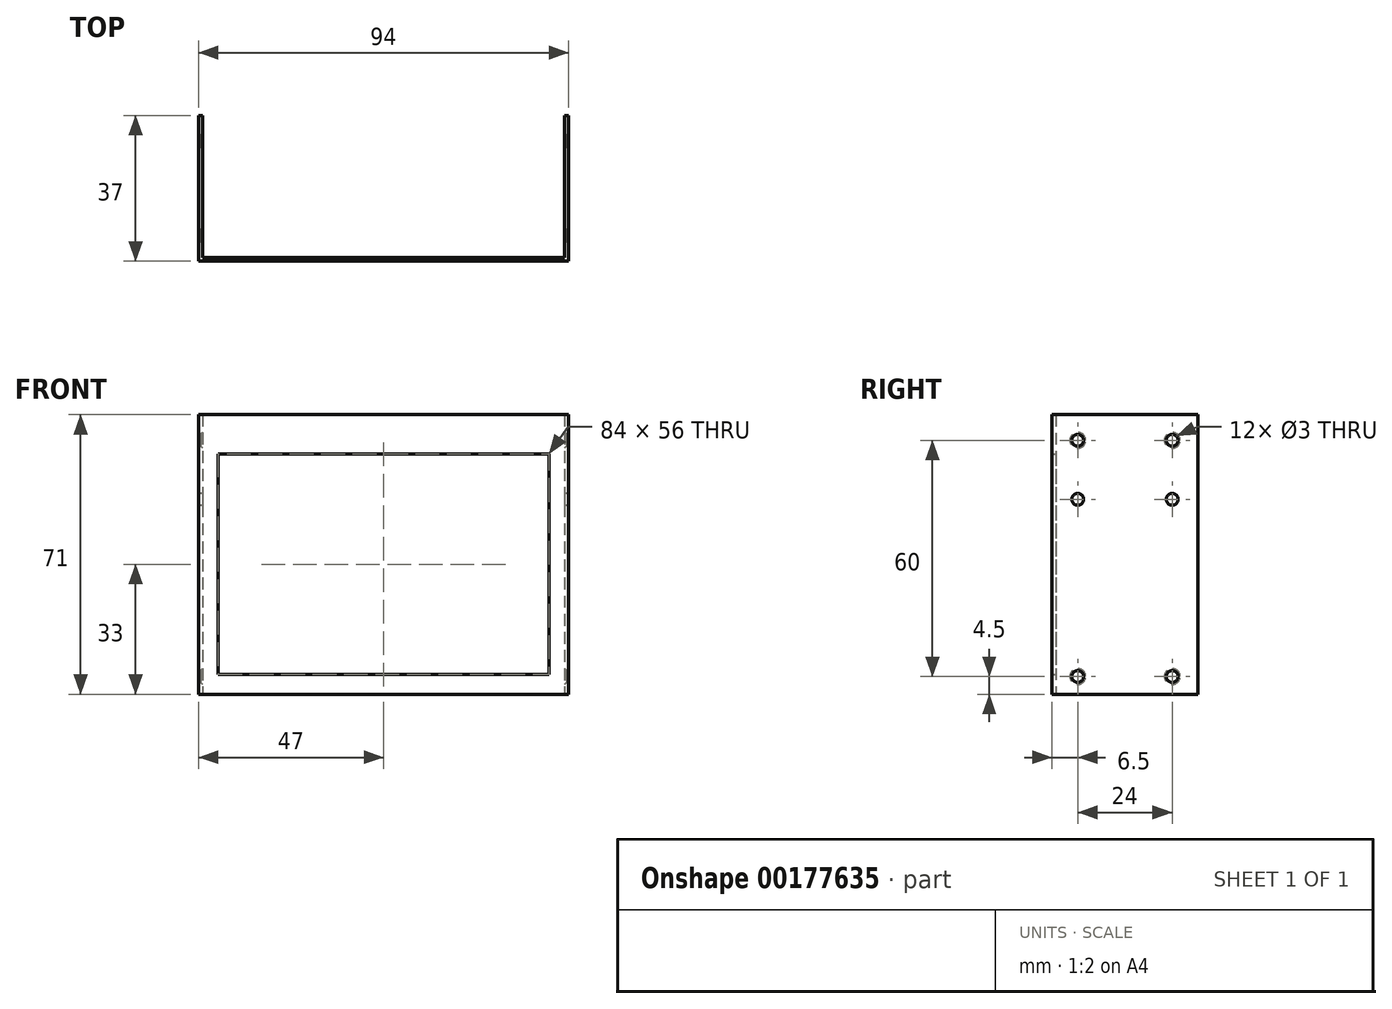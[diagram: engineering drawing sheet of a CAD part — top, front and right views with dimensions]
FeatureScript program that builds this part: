
annotation { "Feature Type Name" : "Feature", "Feature Type Description" : "" }
export const myFeature = defineFeature(function(context is Context, id is Id, definition is map)
    precondition{}
    {
        {
            var Q0;
            Q0=qCreatedBy(makeId("Front.planeOp"),FACE);
            var sketch = newSketch(context, id + "F0", { "sketchPlane" : qUnion([Q0])});
            skLineSegment(sketch, "E0.bottom", {"start": v(47, 35.5) * mm, "end": v(-47, 35.5) * mm});
            skLineSegment(sketch, "E0.top", {"start": v(47, -35.5) * mm, "end": v(-47, -35.5) * mm});
            skLineSegment(sketch, "E0.left", {"start": v(47, 35.5) * mm, "end": v(47, -35.5) * mm});
            skLineSegment(sketch, "E0.right", {"start": v(-47, 35.5) * mm, "end": v(-47, -35.5) * mm});
            skPoint(sketch, "E0.middle", {"position": v(0, 0) * mm});
            skLineSegment(sketch, "E1.bottom", {"start": v(42, 25.5) * mm, "end": v(-42, 25.5) * mm});
            skLineSegment(sketch, "E1.top", {"start": v(42, -30.5) * mm, "end": v(-42, -30.5) * mm});
            skLineSegment(sketch, "E1.left", {"start": v(42, 25.5) * mm, "end": v(42, -30.5) * mm});
            skLineSegment(sketch, "E1.right", {"start": v(-42, 25.5) * mm, "end": v(-42, -30.5) * mm});
            skPoint(sketch, "E1.middle", {"position": v(0, -2.5) * mm});
            skSolve(sketch);
        }
        {
            var Q0;
            Q0=qSketchRegion(id+"F0",true);
            extrude(context, id + "F1", {"entities" : qUnion([Q0]), "depth" : 1 * mm});
        }
        {
            var Q0;
            Q0=makeQuery(id+"F1.opExtrude","CAP_FACE",FACE,{"disambiguationData":[OSD([sQuery(id+"F0.wireOp",EDGE,"E0.bottom"),sQuery(id+"F0.wireOp",EDGE,"E0.top"),sQuery(id+"F0.wireOp",EDGE,"E0.left"),sQuery(id+"F0.wireOp",EDGE,"E0.right"),sQuery(id+"F0.wireOp",EDGE,"SgeA5SFv-ycm6-KkIP-0Kqd-vPRJc91bn5sW.bottom"),sQuery(id+"F0.wireOp",EDGE,"SgeA5SFv-ycm6-KkIP-0Kqd-vPRJc91bn5sW.top"),sQuery(id+"F0.wireOp",EDGE,"SgeA5SFv-ycm6-KkIP-0Kqd-vPRJc91bn5sW.left"),sQuery(id+"F0.wireOp",EDGE,"SgeA5SFv-ycm6-KkIP-0Kqd-vPRJc91bn5sW.right")])],"isStart":true});
            var sketch = newSketch(context, id + "F2", { "sketchPlane" : qUnion([Q0])});
            skLineSegment(sketch, "E2.bottom", {"start": v(-47, 35.5) * mm, "end": v(-46, 35.5) * mm});
            skLineSegment(sketch, "E2.top", {"start": v(-47, -35.5) * mm, "end": v(-46, -35.5) * mm});
            skLineSegment(sketch, "E2.left", {"start": v(-47, 35.5) * mm, "end": v(-47, -35.5) * mm});
            skLineSegment(sketch, "E2.right", {"start": v(-46, 35.5) * mm, "end": v(-46, -35.5) * mm});
            skLineSegment(sketch, "E3.bottom", {"start": v(47, 35.5) * mm, "end": v(46, 35.5) * mm});
            skLineSegment(sketch, "E3.top", {"start": v(47, -35.5) * mm, "end": v(46, -35.5) * mm});
            skLineSegment(sketch, "E3.left", {"start": v(47, 35.5) * mm, "end": v(47, -35.5) * mm});
            skLineSegment(sketch, "E3.right", {"start": v(46, 35.5) * mm, "end": v(46, -35.5) * mm});
            skSolve(sketch);
        }
        {
            var Q0;
            Q0=qSketchRegion(id+"F2",true);
            extrude(context, id + "F3", {"entities" : qUnion([Q0]), "operationType" : NewBodyOperationType.ADD, "depth" : 36 * mm});
        }
        {
            var Q0;
            Q0=makeQuery(id+"F3.boolean.opBoolean","MERGE",FACE,{"derivedFrom":[makeQuery(id+"F1.opExtrude","SWEPT_FACE",FACE,{"disambiguationData":[OSD([sQuery(id+"F0.wireOp",EDGE,"E0.right")])]}),makeQuery(id+"F3.opExtrude","SWEPT_FACE",FACE,{"disambiguationData":[OSD([sQuery(id+"F2.wireOp",EDGE,"E3.left")])]})]});
            var sketch = newSketch(context, id + "F4", { "sketchPlane" : qUnion([Q0])});
            skCircle(sketch, "E4", {"center": v(-29.5, -31) * mm, "radius": 1.5 * mm});
            skCircle(sketch, "E5", {"center": v(-5.5, -31) * mm, "radius": 1.5 * mm});
            skCircle(sketch, "E6", {"center": v(-29.5, 29) * mm, "radius": 1.5 * mm});
            skCircle(sketch, "E7", {"center": v(-5.5, 29) * mm, "radius": 1.5 * mm});
            skLineSegment(sketch, "E8", {"start": v(-29.5, 29) * mm, "end": v(-29.5, -31) * mm, "construction": true});
            skLineSegment(sketch, "E9", {"start": v(-5.5, 29) * mm, "end": v(-5.5, -31) * mm, "construction": true});
            skCircle(sketch, "E10", {"center": v(-29.5, 14) * mm, "radius": 1.5 * mm});
            skCircle(sketch, "E11", {"center": v(-5.5, 14) * mm, "radius": 1.5 * mm});
            skSolve(sketch);
        }
        {
            var Q0;
            Q0=qSketchRegion(id+"F4",true);
            extrude(context, id + "F5", {"entities" : qUnion([Q0]), "operationType" : NewBodyOperationType.REMOVE, "oppositeDirection" : true, "depth" : 100 * mm});
        }
        {
            var Q0;
            Q0=makeQuery(id+"F5.boolean.opBoolean","INTERSECT",EDGE,{"derivedFrom":[makeQuery(id+"F3.opExtrude","SWEPT_FACE",FACE,{"disambiguationData":[OSD([sQuery(id+"F2.wireOp",EDGE,"E3.right")])]}),makeQuery(id+"F5.opExtrude","SWEPT_FACE",FACE,{"disambiguationData":[OSD([sQuery(id+"F4.wireOp",EDGE,"E4")])]})]});
            var Q1;
            Q1=makeQuery(id+"F5.boolean.opBoolean","INTERSECT",EDGE,{"derivedFrom":[makeQuery(id+"F3.opExtrude","SWEPT_FACE",FACE,{"disambiguationData":[OSD([sQuery(id+"F2.wireOp",EDGE,"E3.right")])]}),makeQuery(id+"F5.opExtrude","SWEPT_FACE",FACE,{"disambiguationData":[OSD([sQuery(id+"F4.wireOp",EDGE,"E5")])]})]});
            var Q2;
            Q2=makeQuery(id+"F5.boolean.opBoolean","INTERSECT",EDGE,{"derivedFrom":[makeQuery(id+"F3.opExtrude","SWEPT_FACE",FACE,{"disambiguationData":[OSD([sQuery(id+"F2.wireOp",EDGE,"E2.right")])]}),makeQuery(id+"F5.opExtrude","SWEPT_FACE",FACE,{"disambiguationData":[OSD([sQuery(id+"F4.wireOp",EDGE,"E5")])]})]});
            var Q3;
            Q3=makeQuery(id+"F5.boolean.opBoolean","INTERSECT",EDGE,{"derivedFrom":[makeQuery(id+"F3.opExtrude","SWEPT_FACE",FACE,{"disambiguationData":[OSD([sQuery(id+"F2.wireOp",EDGE,"E2.right")])]}),makeQuery(id+"F5.opExtrude","SWEPT_FACE",FACE,{"disambiguationData":[OSD([sQuery(id+"F4.wireOp",EDGE,"E4")])]})]});
            chamfer(context, id + "F6", {"entities" : qUnion([Q0, Q1, Q2, Q3]), "width" : .5 * mm, "tangentPropagation" : true});
        }
        {
            var Q0;
            Q0=makeQuery(id+"F5.boolean.opBoolean","INTERSECT",EDGE,{"derivedFrom":[makeQuery(id+"F3.opExtrude","SWEPT_FACE",FACE,{"disambiguationData":[OSD([sQuery(id+"F2.wireOp",EDGE,"E2.right")])]}),makeQuery(id+"F5.opExtrude","SWEPT_FACE",FACE,{"disambiguationData":[OSD([sQuery(id+"F4.wireOp",EDGE,"E6")])]})]});
            var Q1;
            Q1=makeQuery(id+"F5.boolean.opBoolean","INTERSECT",EDGE,{"derivedFrom":[makeQuery(id+"F3.opExtrude","SWEPT_FACE",FACE,{"disambiguationData":[OSD([sQuery(id+"F2.wireOp",EDGE,"E2.right")])]}),makeQuery(id+"F5.opExtrude","SWEPT_FACE",FACE,{"disambiguationData":[OSD([sQuery(id+"F4.wireOp",EDGE,"E7")])]})]});
            var Q2;
            Q2=makeQuery(id+"F5.boolean.opBoolean","INTERSECT",EDGE,{"derivedFrom":[makeQuery(id+"F3.opExtrude","SWEPT_FACE",FACE,{"disambiguationData":[OSD([sQuery(id+"F2.wireOp",EDGE,"E3.right")])]}),makeQuery(id+"F5.opExtrude","SWEPT_FACE",FACE,{"disambiguationData":[OSD([sQuery(id+"F4.wireOp",EDGE,"E7")])]})]});
            var Q3;
            Q3=makeQuery(id+"F5.boolean.opBoolean","INTERSECT",EDGE,{"derivedFrom":[makeQuery(id+"F3.opExtrude","SWEPT_FACE",FACE,{"disambiguationData":[OSD([sQuery(id+"F2.wireOp",EDGE,"E3.right")])]}),makeQuery(id+"F5.opExtrude","SWEPT_FACE",FACE,{"disambiguationData":[OSD([sQuery(id+"F4.wireOp",EDGE,"E6")])]})]});
            chamfer(context, id + "F7", {"entities" : qUnion([Q0, Q1, Q2, Q3]), "width" : .5 * mm, "tangentPropagation" : true});
        }
    });
